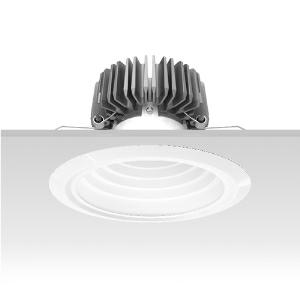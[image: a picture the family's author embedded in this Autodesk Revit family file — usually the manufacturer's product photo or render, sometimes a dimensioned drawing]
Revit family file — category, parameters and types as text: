
# Revit family: 3f_filippi_-_3f_reno_bianco_ampio_3f_filippi_-_30691_a01025_-_3f_reno_200_wh_4000-930_dali_wide___vt_wh_720b
name_source: partatom
category: Lighting Fixtures
units: mm (PartAtom-declared; Revit-internal decimal feet)

## family parameters
Cut with Voids When Loaded = No
Host = Face
Light Source = No
Part Type = Normal
Room Calculation Point = No
Round Connector Dimension = Use Diameter
Shared = No

## types (1)
- 3F Filippi - 3F Reno Bianco Ampio (1 x LED, 3064 lm, 43 W, 3000 K)
    Apparent Load = 43 VA
    Approval mark = CE
    CIE Flux Codes = 75 94 99 100 100
    Color Rendering = 90
    Color Temperature = 3000 K
    Control Gear = Electronic transformer
    Default Elevation = 1800 mm
    Description = ILLUMINOTECHNICAL
Luminous efficiency 100% (DLOR 100%, ULOR 0%).
Initial luminous flux of the luminaire 3064 lm.
Direct symmetric wide distribution.
Installation Interdistance Transv.D = 1.56 x hu - Long.D = 1.56 x hu.
Tabular UGR (CIE 117 - 4H-8H; S=0.25H; 70/50/20): RUG 22.4 - 22.3.
Beam angle: 74° - 74°.
Luminous efficacy 71 lm/W.
Lifetime (L90/B10): 30000 h. (tq+25°C)
Lifetime (L85/B10): 50000 h. (tq+25°C)
Lifetime (L70/B10): 80000 h. (tq+25°C)
Sudden decreased luminous flux after 50000 hours: 0% (C0).
Photobiological safety in compliance with IEC/TR 62778: RG1 low risk, (IEC 62471).
In compliance with IEC/EN 62722-2-1 - IEC/EN 62717 standards.

SOURCE
Compact LED module 4000/930.
Energy efficiency class (UE 2019/2020 - UE 2019/2015): F.
CIE 13.3 Colour rendering index: CRI >90 (R9 >50%).
IES TM-30 Fidelity Index: Rf = 92 Rg = 101.
CCT nominal colour temperature 3000 K.
Colour initial tolerance (MacAdam): SDCM 3.
Zhaga Book 3 compliant.

MECHANICAL
Passive heat dissipator in die-casting aluminium, oversized, for optimum thermal management of the LED module.
Parabolic element with graduated/concentric rings in white polycarbonate.
Transparent external lens with glossy and satin differentiated surfaces, with a cooling and anti-insect system in methacrylate (PMMA).
Fastening spring clips in stainless steel.
Dimensions: diameter 226 mm, height 146 mm. Weight 1.785 kg.
IP44 protection degree for exposed part, IP20 for recessed part.
Mechanical strength to impacts IK06 (1 joule).
Glow-wire test resistance 650°C.

ELECTRICAL
Wiring on a separate unit.
Halogen Free DALI-2 DATI (Parts 251, 252, 253), PUSH-DIM, electronic wiring 230V-50/60Hz, power factor 0.97 at full load, THD <25%, constant output current, SELV, class II, 1 driver, 1 DALI addresse.
Power of the luminaire 43 W.
ENEC - CE.
SAFE FLICKER: PstLM=<1 and SVM=<0.4 (IEC TR 61547-1 and IEC TR 63158), to ensure a more comfortable and safe light.
Luminaire compliant with EN 60598-2-22 for power supply from a centralised emergency system CPSS (Central Power Supply System), not incorporated in the luminaire - high risk areas excluded. The default power and flux are 100% in AC and 100% in DC.
Ambient temperature from 0°C to +25°C.
Temperature class T6 max 85°C.
Relative humidity UR: <85%.

INSTALLATION
Pull-up recessed fitting.
False ceiling carving: 200 mm.
All accessories dedicated to this product are available on the Catalog and on our website www.3F-Filippi.com.

ACCESSORIES
A01025 - VT transparent glass, tempered, not flammable, locked and in line with the trim, in white polycarbonate.

APPLICATIONS
Environments: architectural, commercial, exhibition areas, transit areas, corridors, shops, display windows, service areas.
In false ceilings with narrow voids.

LIGHT MANAGEMENT
Recommended minimum setting: 10%.
The luminaire, equipped with (DALI-2 DATI) driver, can be controlled manually with 3F Easy Dim technology or automatically/manually with wired or wireless DALI/D2D control systems.
The D2D driver guarantees interoperability with other devices with the same certification by making the following information available:
Device Data (Part 251), Energy Report (Part 252), Diagnosis & Maintenance (Part 253).
In electrical systems without a regulation system (manual or automatic) and DALI bus, a suitable jumper must be made on the DA-DA terminals of the appliance.

WARNING
Luminaire designed for disposal/recycling at end-of-life.
Replaceable (LED only) light source by a professional. Replaceable control gear by a professional.
    Height = 0 mm  [stored 0 ft]
    Lamp = 1 x LED
    Lamp Light Flux = 3064 lm
    Lamp Power = 43 W
    Lamp count = 1
    Length = 226 mm
    Lifetime = 50000 h
    Luminous efficacy = 71 lm/W
    Manufacturer = 3F Filippi
    ModVariant = No
    Model = 3F Filippi - 30691+A01025 - 3F Reno 200 WH 4000-930 DALI WIDE + VT WH
    Mounting Place = Ceiling
    Mounting Type = Recessed
    Number of Poles = 1
    OnlyDefault = Yes
    Power Factor = 1
    Product Name = 3F Filippi - 3F Reno Bianco Ampio
    Product group = recessed luminaire
    ProductGroupID = 4
    Protection Class = Protection class II
    Protection Degree = IP 20
    RLX_Detail_Level = 1
    RLX_Emergency_Light_Flux = 0 lm
    RLX_Emergency_Type = 0
    RLX_Emergency_Type_DB = No
    RlxData = <blob elided: 98077 chars, md5=d2dc5dcf>
    Socket = socket
    Standby Power = 0 W
    System Light Flux = 3064 lm
    System Power = 43 W
    Type Comments = Product without accessories
    Type Image = 3ffilippi_3f_reno_200_wh__a01025.jpg
    URL = http://relux.com
    VarID = ---
    Voltage = 0 V
    Weight = 0.00 kg
    Width = 0 mm  [stored 0 ft]

note: [stored X ft] marks values corroborated as IEEE doubles in the binary element streams (Revit-internal decimal feet)

## geometry (parser evidence)
native form markers: Blend x4, Sweep x9
no freeform markers — native parametric forms only
